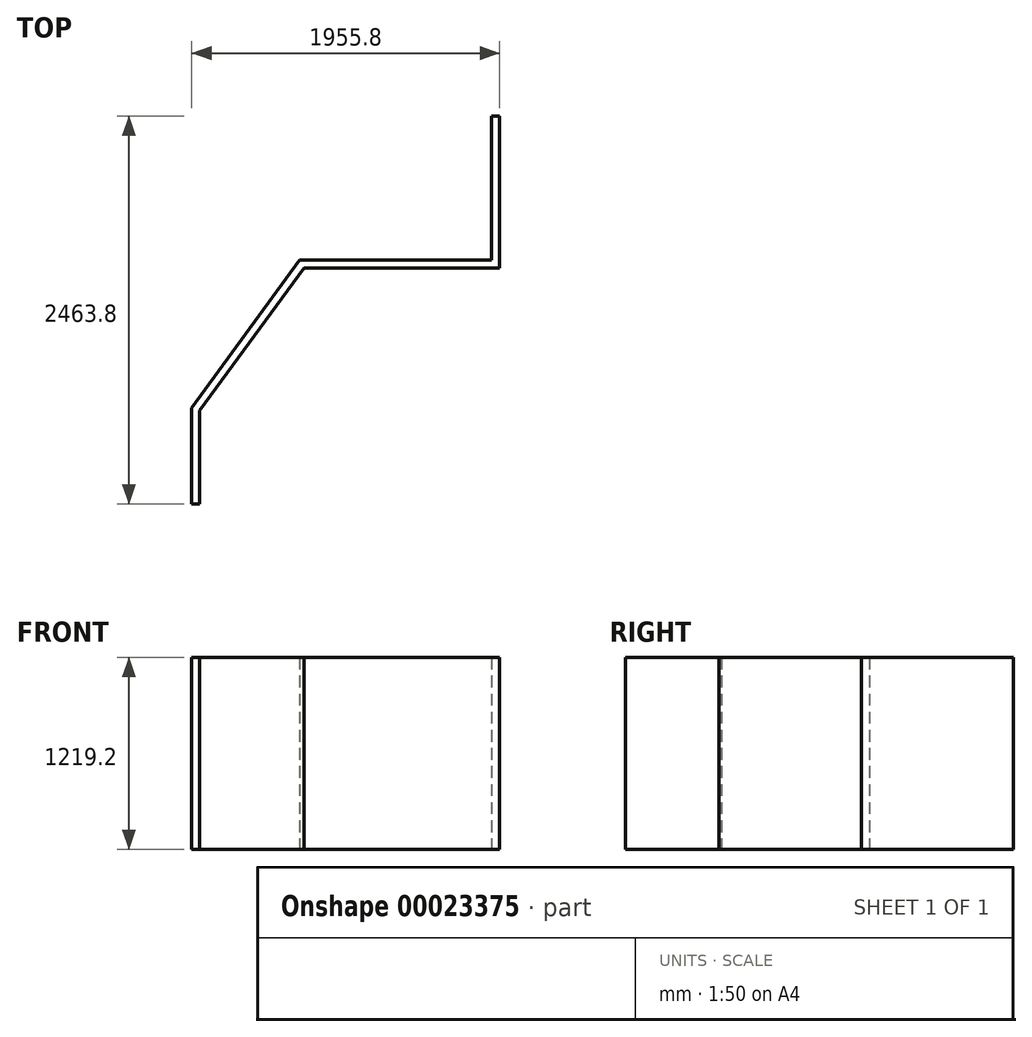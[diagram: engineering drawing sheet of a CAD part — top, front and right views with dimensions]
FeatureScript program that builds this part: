
annotation { "Feature Type Name" : "Feature", "Feature Type Description" : "" }
export const myFeature = defineFeature(function(context is Context, id is Id, definition is map)
    precondition{}
    {
        {
            var Q0;
            Q0=qCreatedBy(makeId("Top.planeOp"),FACE);
            var sketch = newSketch(context, id + "F0", { "sketchPlane" : qUnion([Q0])});
            skLineSegment(sketch, "E0", {"start": v(-1905, -1549.4) * mm, "end": v(-1905, -939.8) * mm});
            skLineSegment(sketch, "E1", {"start": v(-1905, -939.8) * mm, "end": v(-1219.2, 0) * mm});
            skLineSegment(sketch, "E2", {"start": v(-1219.2, 0) * mm, "end": v(0, 0) * mm});
            skLineSegment(sketch, "E3", {"start": v(0, 0) * mm, "end": v(0, 914.4) * mm});
            skLineSegment(sketch, "E4", {"start": v(0, 914.4) * mm, "end": v(50.8, 914.4) * mm});
            skLineSegment(sketch, "E5", {"start": v(50.8, 914.4) * mm, "end": v(50.8, -50.8) * mm});
            skLineSegment(sketch, "E6", {"start": v(50.8, -50.8) * mm, "end": v(-1193.38, -50.8) * mm});
            skLineSegment(sketch, "E7", {"start": v(-1193.38, -50.8) * mm, "end": v(-1854.2, -956.36) * mm});
            skLineSegment(sketch, "E8", {"start": v(-1854.2, -956.36) * mm, "end": v(-1854.2, -1549.4) * mm});
            skLineSegment(sketch, "E9", {"start": v(-1854.2, -1549.4) * mm, "end": v(-1905, -1549.4) * mm});
            skSolve(sketch);
        }
        {
            var Q0;
            Q0 = qSketchRegion(id + "F0", true);
            extrude(context, id + "F1", {"entities" : qUnion([Q0]), "endBound" : BoundingType.SYMMETRIC, "depth" : 1219.2 * mm});
        }
    });
